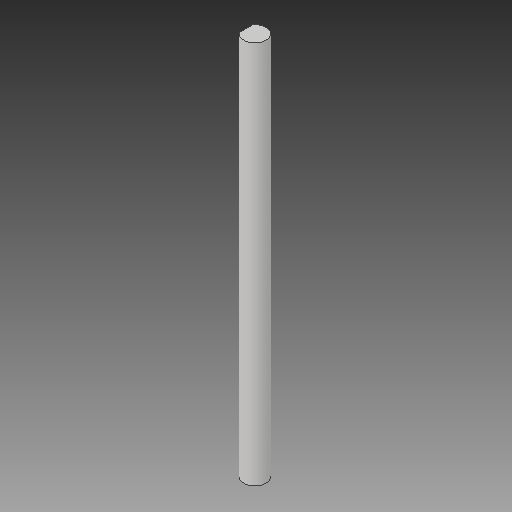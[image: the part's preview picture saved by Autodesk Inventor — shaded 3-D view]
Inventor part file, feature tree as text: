
AUTODESK INVENTOR PART (.ipt)
format: ipt  version: 2017 (Build 210142000, 142)  size: 121,856 bytes
history: native  units: in
note: dims shown in document units (in); Inventor stores cm internally (conversion verified against a paired STEP export)
features: move_body x3, sketch x2, direct_edit x2, extrude x1, projected_geometry x1, chamfer x1
ambient origin geometry x8: Origin, YZ Plane, XZ Plane, XY Plane, X Axis, Y Axis, Z Axis, Center Point
bodies: Solid1 (feature_tree)
feature tree (10):
  extrude  "Extrusion1"  TaperAngle=0.0deg  [1 undecoded]
  sketch  "Sketch2"  dims[d11=0.0in d12=0.0in d13=0.284in]
  direct_edit  "Direct Edit2"
  direct_edit  "Direct Edit3"
  sketch  "Sketch1"  dims[d0=0.83in d1=0.0in d5=0.0in d6=0.0in d7=-0.284in d8=0.0in d9=0.0in d10=-0.284in]
  projected_geometry  "Projected Loop1"
  chamfer  "Chamfer1"  [1 undecoded]
  move_body  "Move2"
  move_body  "Move3"
  move_body  "Move4"
note: 2 required parameter values undecoded (feature->parameter linkage not recoverable at this tier; creation-order binding heuristic only, values carry confidence <= 0.55)
